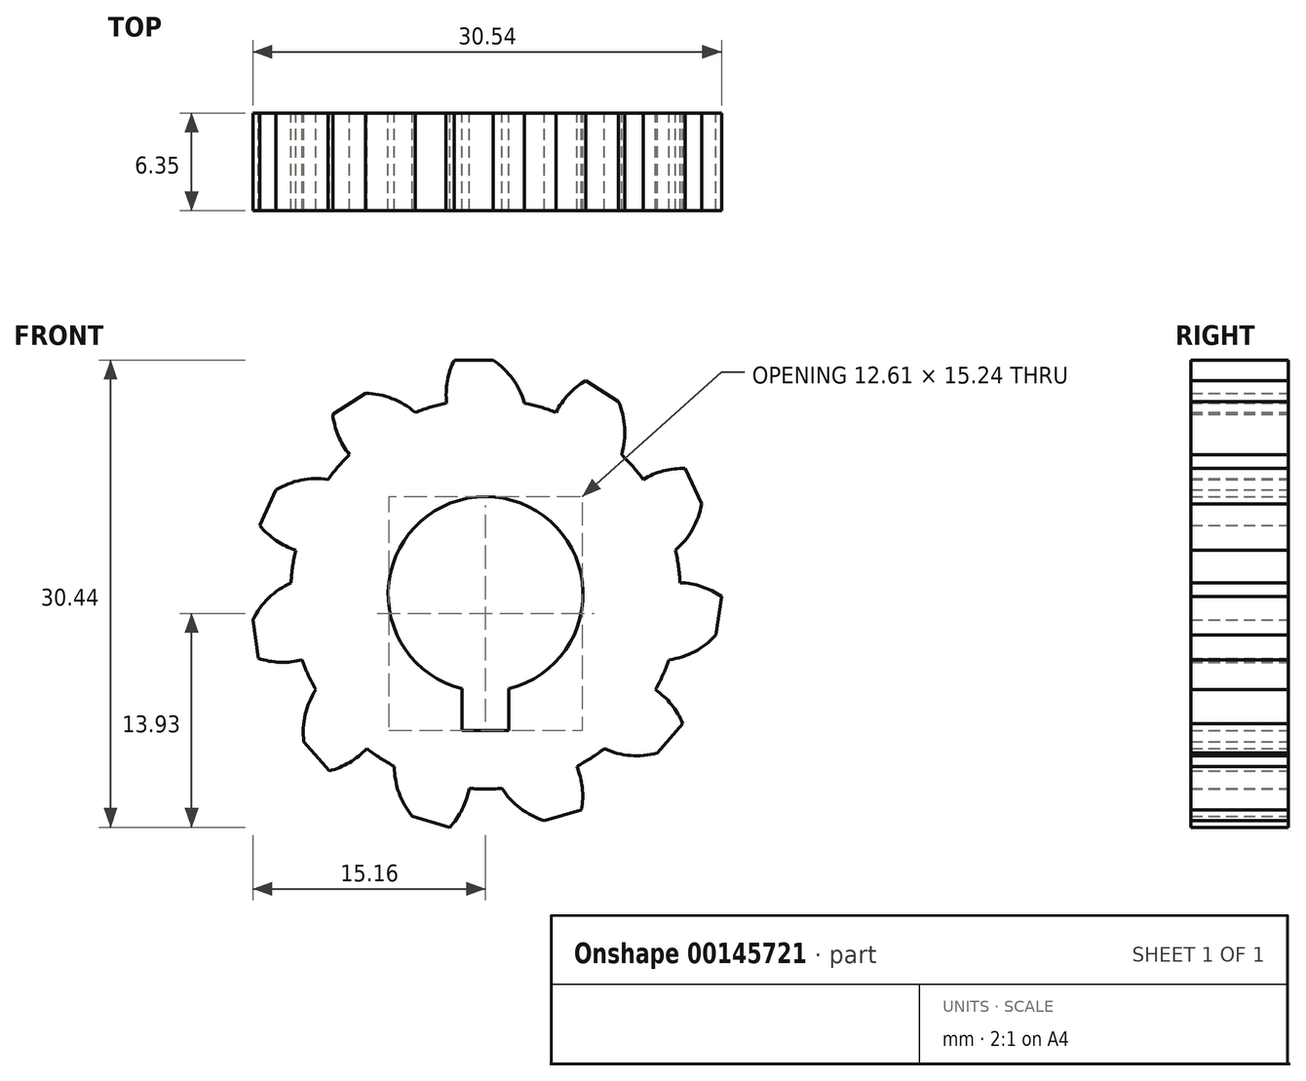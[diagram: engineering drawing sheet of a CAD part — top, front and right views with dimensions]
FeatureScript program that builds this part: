
annotation { "Feature Type Name" : "Feature", "Feature Type Description" : "" }
export const myFeature = defineFeature(function(context is Context, id is Id, definition is map)
    precondition{}
    {
        {
            var Q0;
            Q0=qCreatedBy(makeId("Front.planeOp"),FACE);
            var sketch = newSketch(context, id + "F0", { "sketchPlane" : qUnion([Q0])});
            skArc(sketch, "E0", {"start": v(10.26, 7.48) * mm, "mid": v(9.6, 8.32) * mm, "end": v(8.86, 9.1) * mm, "construction": true});
            skArc(sketch, "E1", {"start": v(-2.04, 15.24) * mm, "mid": v(-2.5, 13.88) * mm, "end": v(-2.54, 12.44) * mm});
            skLineSegment(sketch, "E2", {"start": v(-2.04, 15.24) * mm, "end": v(0.5, 15.24) * mm});
            skArc(sketch, "E3", {"start": v(2.54, 12.44) * mm, "mid": v(1.76, 14.02) * mm, "end": v(0.5, 15.24) * mm});
            skLineSegment(sketch, "E4", {"start": v(0, 15.24) * mm, "end": v(0, 0) * mm, "construction": true});
            skArc(sketch, "E5.1.0", {"start": v(-9.96, 11.72) * mm, "mid": v(-9.6, 10.33) * mm, "end": v(-8.86, 9.1) * mm});
            skLineSegment(sketch, "E5.1.1", {"start": v(-9.96, 11.72) * mm, "end": v(-7.82, 13.1) * mm});
            skArc(sketch, "E5.1.2", {"start": v(-4.6, 11.84) * mm, "mid": v(-6.1, 12.75) * mm, "end": v(-7.82, 13.1) * mm});
            skArc(sketch, "E5.2.0", {"start": v(-14.71, 4.47) * mm, "mid": v(-13.66, 3.5) * mm, "end": v(-12.37, 2.86) * mm});
            skLineSegment(sketch, "E5.2.1", {"start": v(-14.71, 4.47) * mm, "end": v(-13.66, 6.78) * mm});
            skArc(sketch, "E5.2.2", {"start": v(-10.26, 7.48) * mm, "mid": v(-12.02, 7.43) * mm, "end": v(-13.66, 6.78) * mm});
            skArc(sketch, "E5.3.0", {"start": v(-14.8, -4.19) * mm, "mid": v(-13.38, -4.44) * mm, "end": v(-11.96, -4.29) * mm});
            skLineSegment(sketch, "E5.3.1", {"start": v(-14.8, -4.19) * mm, "end": v(-15.16, -1.68) * mm});
            skArc(sketch, "E5.3.2", {"start": v(-12.68, 0.74) * mm, "mid": v(-14.13, -0.25) * mm, "end": v(-15.16, -1.68) * mm});
            skArc(sketch, "E5.4.0", {"start": v(-10.18, -11.52) * mm, "mid": v(-8.86, -10.97) * mm, "end": v(-7.74, -10.07) * mm});
            skLineSegment(sketch, "E5.4.1", {"start": v(-10.18, -11.52) * mm, "end": v(-11.84, -9.6) * mm});
            skArc(sketch, "E5.4.2", {"start": v(-11.07, -6.23) * mm, "mid": v(-11.75, -7.85) * mm, "end": v(-11.84, -9.6) * mm});
            skArc(sketch, "E5.5.0", {"start": v(-2.34, -15.2) * mm, "mid": v(-1.52, -14.02) * mm, "end": v(-1.07, -12.65) * mm});
            skLineSegment(sketch, "E5.5.1", {"start": v(-2.34, -15.2) * mm, "end": v(-4.77, -14.48) * mm});
            skArc(sketch, "E5.5.2", {"start": v(-5.94, -11.22) * mm, "mid": v(-5.64, -12.96) * mm, "end": v(-4.77, -14.48) * mm});
            skArc(sketch, "E6", {"start": v(-8.86, 9.1) * mm, "mid": v(-9.6, 8.32) * mm, "end": v(-10.26, 7.48) * mm});
            skArc(sketch, "E7.trimOffspring", {"start": v(-2.54, 12.44) * mm, "mid": v(-3.58, 12.19) * mm, "end": v(-4.6, 11.84) * mm});
            skArc(sketch, "E8.trimOffspring", {"start": v(4.6, 11.84) * mm, "mid": v(3.58, 12.19) * mm, "end": v(2.54, 12.44) * mm});
            skArc(sketch, "E9.trimOffspring", {"start": v(-7.74, -10.07) * mm, "mid": v(-6.87, -10.68) * mm, "end": v(-5.94, -11.22) * mm});
            skArc(sketch, "E10.trimOffspring", {"start": v(-11.96, -4.29) * mm, "mid": v(-11.55, -5.28) * mm, "end": v(-11.07, -6.23) * mm});
            skArc(sketch, "E11.trimOffspring", {"start": v(-12.37, 2.86) * mm, "mid": v(-12.57, 1.8) * mm, "end": v(-12.68, 0.74) * mm});
            skArc(sketch, "E12.3.6.0", {"start": v(6.25, -14.05) * mm, "mid": v(6.3, -12.61) * mm, "end": v(5.94, -11.22) * mm});
            skLineSegment(sketch, "E12.4.6.0", {"start": v(6.25, -14.05) * mm, "end": v(3.82, -14.76) * mm});
            skArc(sketch, "E12.7.6.0", {"start": v(1.07, -12.65) * mm, "mid": v(2.26, -13.95) * mm, "end": v(3.82, -14.76) * mm});
            skArc(sketch, "E12.3.7.0", {"start": v(12.85, -8.44) * mm, "mid": v(12.12, -7.2) * mm, "end": v(11.07, -6.23) * mm});
            skLineSegment(sketch, "E12.4.7.0", {"start": v(12.85, -8.44) * mm, "end": v(11.2, -10.36) * mm});
            skArc(sketch, "E12.7.7.0", {"start": v(7.74, -10.07) * mm, "mid": v(9.44, -10.52) * mm, "end": v(11.2, -10.36) * mm});
            skArc(sketch, "E12.3.8.0", {"start": v(15.38, -0.15) * mm, "mid": v(14.1, 0.49) * mm, "end": v(12.68, 0.74) * mm});
            skLineSegment(sketch, "E12.4.8.0", {"start": v(15.38, -0.15) * mm, "end": v(15.01, -2.66) * mm});
            skArc(sketch, "E12.7.8.0", {"start": v(11.96, -4.29) * mm, "mid": v(13.63, -3.74) * mm, "end": v(15.01, -2.66) * mm});
            skArc(sketch, "E12.3.9.0", {"start": v(13.01, 8.19) * mm, "mid": v(11.59, 8.03) * mm, "end": v(10.26, 7.48) * mm});
            skLineSegment(sketch, "E12.4.9.0", {"start": v(13.01, 8.19) * mm, "end": v(14.07, 5.88) * mm});
            skArc(sketch, "E12.7.9.0", {"start": v(12.37, 2.86) * mm, "mid": v(13.49, 4.22) * mm, "end": v(14.07, 5.88) * mm});
            skArc(sketch, "E12.3.10.0", {"start": v(6.52, 13.92) * mm, "mid": v(5.4, 13.02) * mm, "end": v(4.6, 11.84) * mm});
            skLineSegment(sketch, "E12.4.10.0", {"start": v(6.52, 13.92) * mm, "end": v(8.66, 12.55) * mm});
            skArc(sketch, "E12.7.10.0", {"start": v(8.86, 9.1) * mm, "mid": v(9.07, 10.84) * mm, "end": v(8.66, 12.55) * mm});
            skCircle(sketch, "E13", {"center": v(0, 0) * mm, "radius": 6.35 * mm});
            skLineSegment(sketch, "E14", {"start": v(-1.52, -6.16) * mm, "end": v(-1.52, -8.9) * mm});
            skLineSegment(sketch, "E15", {"start": v(-1.52, -8.9) * mm, "end": v(0, -8.9) * mm});
            skLineSegment(sketch, "E16", {"start": v(0, -8.9) * mm, "end": v(1.52, -8.9) * mm});
            skLineSegment(sketch, "E17", {"start": v(1.52, -8.9) * mm, "end": v(1.52, -6.16) * mm});
            skLineSegment(sketch, "E18", {"start": v(0, -8.9) * mm, "end": v(0, 0) * mm, "construction": true});
            skArc(sketch, "E19.trimOffspring", {"start": v(10.26, 7.48) * mm, "mid": v(9.6, 8.32) * mm, "end": v(8.86, 9.1) * mm});
            skArc(sketch, "E20.trimOffspring", {"start": v(12.68, 0.74) * mm, "mid": v(12.57, 1.8) * mm, "end": v(12.37, 2.86) * mm, "construction": true});
            skArc(sketch, "E21.trimOffspring", {"start": v(12.68, 0.74) * mm, "mid": v(12.57, 1.8) * mm, "end": v(12.37, 2.86) * mm});
            skArc(sketch, "E22.trimOffspring", {"start": v(11.07, -6.23) * mm, "mid": v(11.55, -5.28) * mm, "end": v(11.96, -4.29) * mm, "construction": true});
            skArc(sketch, "E23.trimOffspring", {"start": v(11.07, -6.23) * mm, "mid": v(11.55, -5.28) * mm, "end": v(11.96, -4.29) * mm});
            skArc(sketch, "E24.trimOffspring", {"start": v(5.94, -11.22) * mm, "mid": v(6.87, -10.68) * mm, "end": v(7.74, -10.07) * mm});
            skArc(sketch, "E25.trimOffspring", {"start": v(-1.07, -12.65) * mm, "mid": v(0, -12.7) * mm, "end": v(1.07, -12.65) * mm, "construction": true});
            skArc(sketch, "E26.trimOffspring", {"start": v(-1.07, -12.65) * mm, "mid": v(0, -12.7) * mm, "end": v(1.07, -12.65) * mm});
            skArc(sketch, "E27.trimOffspring", {"start": v(-11.96, -4.29) * mm, "mid": v(-11.55, -5.28) * mm, "end": v(-11.07, -6.23) * mm, "construction": true});
            skArc(sketch, "E28.trimOffspring", {"start": v(-12.37, 2.86) * mm, "mid": v(-12.57, 1.8) * mm, "end": v(-12.68, 0.74) * mm, "construction": true});
            skArc(sketch, "E29.trimOffspring", {"start": v(-8.86, 9.1) * mm, "mid": v(-9.6, 8.32) * mm, "end": v(-10.26, 7.48) * mm, "construction": true});
            skArc(sketch, "E30.trimOffspring", {"start": v(-2.54, 12.44) * mm, "mid": v(-3.58, 12.19) * mm, "end": v(-4.6, 11.84) * mm, "construction": true});
            skArc(sketch, "E31.trimOffspring", {"start": v(4.6, 11.84) * mm, "mid": v(3.58, 12.19) * mm, "end": v(2.54, 12.44) * mm, "construction": true});
            skSolve(sketch);
        }
        {
            var Q0;
            Q0 = qSketchRegion(id + "F0", true);
            extrude(context, id + "F1", {"entities" : qUnion([Q0]), "depth" : 6.35 * mm});
        }
    });
